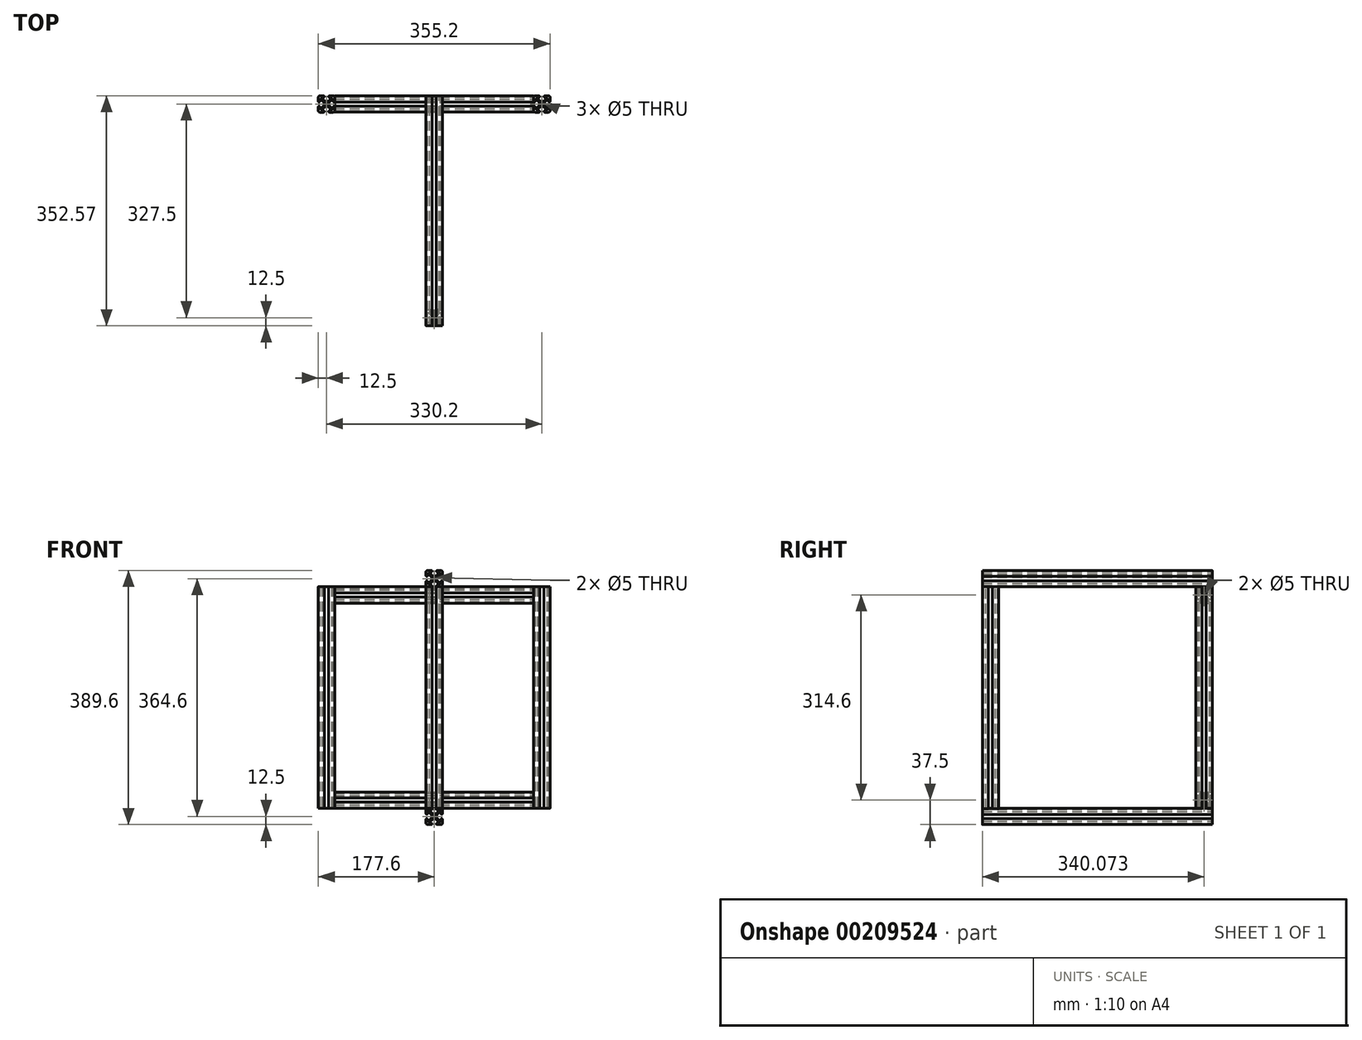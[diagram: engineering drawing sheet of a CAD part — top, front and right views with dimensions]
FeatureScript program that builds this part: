
annotation { "Feature Type Name" : "Feature", "Feature Type Description" : "" }
export const myFeature = defineFeature(function(context is Context, id is Id, definition is map)
    precondition{}
    {
        {
            var Q0;
            Q0=qCreatedBy(makeId("Top.planeOp"),FACE);
            var sketch = newSketch(context, id + "F0", { "sketchPlane" : qUnion([Q0])});
            skCircle(sketch, "E0", {"center": v(0, 0) * mm, "radius": 2.5 * mm});
            skLineSegment(sketch, "E1", {"start": v(0, 0) * mm, "end": v(0, 4.05) * mm, "construction": true});
            skLineSegment(sketch, "E2", {"start": v(0, 0) * mm, "end": v(-4.05, 0) * mm, "construction": true});
            skLineSegment(sketch, "E3", {"start": v(0, 0) * mm, "end": v(-12.5, 12.5) * mm, "construction": true});
            skLineSegment(sketch, "E4", {"start": v(-12.5, 10.36) * mm, "end": v(-12.5, 4.32) * mm});
            skLineSegment(sketch, "E5", {"start": v(-10.36, 12.5) * mm, "end": v(-4.32, 12.5) * mm});
            skLineSegment(sketch, "E6", {"start": v(-4.32, 10.36) * mm, "end": v(-6.26, 10.36) * mm});
            skLineSegment(sketch, "E7", {"start": v(-10.36, 6.26) * mm, "end": v(-10.36, 4.32) * mm});
            skArc(sketch, "E8", {"start": v(-4.32, 12.5) * mm, "mid": v(-3.25, 11.43) * mm, "end": v(-4.32, 10.36) * mm});
            skArc(sketch, "E9", {"start": v(-10.36, 4.32) * mm, "mid": v(-11.43, 3.25) * mm, "end": v(-12.5, 4.32) * mm});
            skLineSegment(sketch, "E10", {"start": v(0, 4.05) * mm, "end": v(-2.1, 4.05) * mm});
            skLineSegment(sketch, "E11", {"start": v(-4.05, 2.1) * mm, "end": v(-4.05, 0) * mm});
            skLineSegment(sketch, "E12", {"start": v(-8.53, 7.02) * mm, "end": v(-4.36, 2.85) * mm});
            skLineSegment(sketch, "E13", {"start": v(-7.02, 8.53) * mm, "end": v(-2.85, 4.36) * mm});
            skLineSegment(sketch, "E14.0.MirrorCS", {"start": v(10.36, 6.26) * mm, "end": v(10.36, 4.32) * mm});
            skLineSegment(sketch, "E14.1.MirrorCS", {"start": v(7.02, 8.53) * mm, "end": v(2.85, 4.36) * mm});
            skArc(sketch, "E14.2.MirrorCS", {"start": v(4.32, 12.5) * mm, "mid": v(3.25, 11.43) * mm, "end": v(4.32, 10.36) * mm});
            skArc(sketch, "E14.3.MirrorCS", {"start": v(10.36, 4.32) * mm, "mid": v(11.43, 3.25) * mm, "end": v(12.5, 4.32) * mm});
            skLineSegment(sketch, "E14.4.MirrorCS", {"start": v(10.36, 12.5) * mm, "end": v(4.32, 12.5) * mm});
            skLineSegment(sketch, "E14.5.MirrorCS", {"start": v(4.32, 10.36) * mm, "end": v(6.26, 10.36) * mm});
            skLineSegment(sketch, "E14.6.MirrorCS", {"start": v(12.5, 10.36) * mm, "end": v(12.5, 4.32) * mm});
            skLineSegment(sketch, "E14.7.MirrorCS", {"start": v(8.53, 7.02) * mm, "end": v(4.36, 2.85) * mm});
            skLineSegment(sketch, "E15.0.MirrorCS", {"start": v(0, 4.05) * mm, "end": v(2.1, 4.05) * mm});
            skLineSegment(sketch, "E16.0.MirrorCS", {"start": v(4.05, 2.1) * mm, "end": v(4.05, 0) * mm});
            skLineSegment(sketch, "E17.0.MirrorCS", {"start": v(10.36, -12.5) * mm, "end": v(4.32, -12.5) * mm});
            skLineSegment(sketch, "E17.1.MirrorCS", {"start": v(12.5, -10.36) * mm, "end": v(12.5, -4.32) * mm});
            skArc(sketch, "E17.2.MirrorCS", {"start": v(4.32, -12.5) * mm, "mid": v(3.25, -11.43) * mm, "end": v(4.32, -10.36) * mm});
            skLineSegment(sketch, "E17.3.MirrorCS", {"start": v(-7.02, -8.53) * mm, "end": v(-2.85, -4.36) * mm});
            skLineSegment(sketch, "E17.4.MirrorCS", {"start": v(7.02, -8.53) * mm, "end": v(2.85, -4.36) * mm});
            skLineSegment(sketch, "E17.5.MirrorCS", {"start": v(10.36, -6.26) * mm, "end": v(10.36, -4.32) * mm});
            skLineSegment(sketch, "E17.6.MirrorCS", {"start": v(8.53, -7.02) * mm, "end": v(4.36, -2.85) * mm});
            skLineSegment(sketch, "E17.7.MirrorCS", {"start": v(-10.36, -12.5) * mm, "end": v(-4.32, -12.5) * mm});
            skLineSegment(sketch, "E17.8.MirrorCS", {"start": v(-4.32, -10.36) * mm, "end": v(-6.26, -10.36) * mm});
            skLineSegment(sketch, "E17.9.MirrorCS", {"start": v(4.32, -10.36) * mm, "end": v(6.26, -10.36) * mm});
            skArc(sketch, "E17.10.MirrorCS", {"start": v(10.36, -4.32) * mm, "mid": v(11.43, -3.25) * mm, "end": v(12.5, -4.32) * mm});
            skLineSegment(sketch, "E17.11.MirrorCS", {"start": v(-12.5, -10.36) * mm, "end": v(-12.5, -4.32) * mm});
            skLineSegment(sketch, "E17.12.MirrorCS", {"start": v(0, -4.05) * mm, "end": v(2.1, -4.05) * mm});
            skArc(sketch, "E17.13.MirrorCS", {"start": v(-4.32, -12.5) * mm, "mid": v(-3.25, -11.43) * mm, "end": v(-4.32, -10.36) * mm});
            skLineSegment(sketch, "E17.14.MirrorCS", {"start": v(-8.53, -7.02) * mm, "end": v(-4.36, -2.85) * mm});
            skArc(sketch, "E17.15.MirrorCS", {"start": v(-10.36, -4.32) * mm, "mid": v(-11.43, -3.25) * mm, "end": v(-12.5, -4.32) * mm});
            skLineSegment(sketch, "E17.16.MirrorCS", {"start": v(-10.36, -6.26) * mm, "end": v(-10.36, -4.32) * mm});
            skLineSegment(sketch, "E17.17.MirrorCS", {"start": v(0, -4.05) * mm, "end": v(-2.1, -4.05) * mm});
            skLineSegment(sketch, "E18.0.MirrorCS", {"start": v(4.05, -2.1) * mm, "end": v(4.05, 0) * mm});
            skLineSegment(sketch, "E19.0.MirrorCS", {"start": v(-4.05, -2.1) * mm, "end": v(-4.05, 0) * mm});
            skPoint(sketch, "E20.visualSharp", {"position": v(-12.5, 12.5) * mm});
            skArc(sketch, "E20.filletArc", {"start": v(-10.36, 12.5) * mm, "mid": v(-11.87, 11.87) * mm, "end": v(-12.5, 10.36) * mm});
            skPoint(sketch, "E21.visualSharp", {"position": v(12.5, 12.5) * mm});
            skArc(sketch, "E21.filletArc", {"start": v(12.5, 10.36) * mm, "mid": v(11.87, 11.87) * mm, "end": v(10.36, 12.5) * mm});
            skPoint(sketch, "E22.visualSharp", {"position": v(12.5, -12.5) * mm});
            skArc(sketch, "E22.filletArc", {"start": v(10.36, -12.5) * mm, "mid": v(11.87, -11.87) * mm, "end": v(12.5, -10.36) * mm});
            skPoint(sketch, "E23.visualSharp", {"position": v(-12.5, -12.5) * mm});
            skArc(sketch, "E23.filletArc", {"start": v(-12.5, -10.36) * mm, "mid": v(-11.87, -11.87) * mm, "end": v(-10.36, -12.5) * mm});
            skPoint(sketch, "E24.visualSharp", {"position": v(4.05, 4.05) * mm});
            skPoint(sketch, "E25.visualSharp", {"position": v(-10.36, 8.85) * mm});
            skArc(sketch, "E25.filletArc", {"start": v(-8.53, 7.02) * mm, "mid": v(-9.7, 7.25) * mm, "end": v(-10.36, 6.26) * mm});
            skPoint(sketch, "E26.visualSharp", {"position": v(-8.85, 10.36) * mm});
            skArc(sketch, "E26.filletArc", {"start": v(-6.26, 10.36) * mm, "mid": v(-7.25, 9.7) * mm, "end": v(-7.02, 8.53) * mm});
            skPoint(sketch, "E27.visualSharp", {"position": v(8.85, 10.36) * mm});
            skArc(sketch, "E27.filletArc", {"start": v(7.02, 8.53) * mm, "mid": v(7.25, 9.7) * mm, "end": v(6.26, 10.36) * mm});
            skPoint(sketch, "E28.visualSharp", {"position": v(10.36, 8.85) * mm});
            skArc(sketch, "E28.filletArc", {"start": v(10.36, 6.26) * mm, "mid": v(9.7, 7.25) * mm, "end": v(8.53, 7.02) * mm});
            skPoint(sketch, "E29.visualSharp", {"position": v(10.36, -8.85) * mm});
            skArc(sketch, "E29.filletArc", {"start": v(8.53, -7.02) * mm, "mid": v(9.7, -7.25) * mm, "end": v(10.36, -6.26) * mm});
            skPoint(sketch, "E30.visualSharp", {"position": v(8.85, -10.36) * mm});
            skArc(sketch, "E30.filletArc", {"start": v(6.26, -10.36) * mm, "mid": v(7.25, -9.7) * mm, "end": v(7.02, -8.53) * mm});
            skPoint(sketch, "E31.visualSharp", {"position": v(-8.85, -10.36) * mm});
            skArc(sketch, "E31.filletArc", {"start": v(-7.02, -8.53) * mm, "mid": v(-7.25, -9.7) * mm, "end": v(-6.26, -10.36) * mm});
            skPoint(sketch, "E32.visualSharp", {"position": v(-10.36, -8.85) * mm});
            skArc(sketch, "E32.filletArc", {"start": v(-10.36, -6.26) * mm, "mid": v(-9.7, -7.25) * mm, "end": v(-8.53, -7.02) * mm});
            skPoint(sketch, "E33.orphan", {"position": v(-4.05, 4.05) * mm});
            skPoint(sketch, "E34.orphan", {"position": v(4.05, -4.05) * mm});
            skPoint(sketch, "E35.orphan", {"position": v(-4.05, -4.05) * mm});
            skPoint(sketch, "E36.visualSharp", {"position": v(-2.54, 4.05) * mm});
            skArc(sketch, "E36.filletArc", {"start": v(-2.85, 4.36) * mm, "mid": v(-2.5, 4.13) * mm, "end": v(-2.1, 4.05) * mm});
            skPoint(sketch, "E37.visualSharp", {"position": v(2.54, 4.05) * mm});
            skArc(sketch, "E37.filletArc", {"start": v(2.1, 4.05) * mm, "mid": v(2.5, 4.13) * mm, "end": v(2.85, 4.36) * mm});
            skPoint(sketch, "E38.visualSharp", {"position": v(-4.05, 2.54) * mm});
            skArc(sketch, "E38.filletArc", {"start": v(-4.05, 2.1) * mm, "mid": v(-4.13, 2.5) * mm, "end": v(-4.36, 2.85) * mm});
            skPoint(sketch, "E39.visualSharp", {"position": v(-4.05, -2.54) * mm});
            skArc(sketch, "E39.filletArc", {"start": v(-4.36, -2.85) * mm, "mid": v(-4.13, -2.5) * mm, "end": v(-4.05, -2.1) * mm});
            skPoint(sketch, "E40.visualSharp", {"position": v(-2.54, -4.05) * mm});
            skArc(sketch, "E40.filletArc", {"start": v(-2.1, -4.05) * mm, "mid": v(-2.5, -4.13) * mm, "end": v(-2.85, -4.36) * mm});
            skPoint(sketch, "E41.visualSharp", {"position": v(2.54, -4.05) * mm});
            skArc(sketch, "E41.filletArc", {"start": v(2.85, -4.36) * mm, "mid": v(2.5, -4.13) * mm, "end": v(2.1, -4.05) * mm});
            skPoint(sketch, "E42.visualSharp", {"position": v(4.05, -2.54) * mm});
            skArc(sketch, "E42.filletArc", {"start": v(4.05, -2.1) * mm, "mid": v(4.13, -2.5) * mm, "end": v(4.36, -2.85) * mm});
            skPoint(sketch, "E43.visualSharp", {"position": v(4.05, 2.54) * mm});
            skArc(sketch, "E43.filletArc", {"start": v(4.36, 2.85) * mm, "mid": v(4.13, 2.5) * mm, "end": v(4.05, 2.1) * mm});
            skSolve(sketch);
        }
        {
            var Q0;
            Q0=qSketchRegion(id+"F0",true);
            extrude(context, id + "F1", {"entities" : qUnion([Q0]), "endBound" : BoundingType.SYMMETRIC, "depth" : 340 * mm});
        }
        {
            var Q0;
            Q0=qCreatedBy(makeId("Top.planeOp"),FACE);
            var sketch = newSketch(context, id + "F2", { "sketchPlane" : qUnion([Q0])});
            skCircle(sketch, "E44", {"center": v(330.2, 0) * mm, "radius": 2.5 * mm});
            skLineSegment(sketch, "E45", {"start": v(330.2, 0) * mm, "end": v(330.2, 4.05) * mm, "construction": true});
            skLineSegment(sketch, "E46", {"start": v(330.2, 0) * mm, "end": v(326.15, 0) * mm, "construction": true});
            skLineSegment(sketch, "E47", {"start": v(330.2, 0) * mm, "end": v(317.7, 12.5) * mm, "construction": true});
            skLineSegment(sketch, "E48", {"start": v(317.7, 10.36) * mm, "end": v(317.7, 4.32) * mm});
            skLineSegment(sketch, "E49", {"start": v(319.84, 12.5) * mm, "end": v(325.88, 12.5) * mm});
            skLineSegment(sketch, "E50", {"start": v(325.88, 10.36) * mm, "end": v(323.94, 10.36) * mm});
            skLineSegment(sketch, "E51", {"start": v(319.84, 6.26) * mm, "end": v(319.84, 4.32) * mm});
            skArc(sketch, "E52", {"start": v(325.88, 12.5) * mm, "mid": v(326.95, 11.43) * mm, "end": v(325.88, 10.36) * mm});
            skArc(sketch, "E53", {"start": v(319.84, 4.32) * mm, "mid": v(318.77, 3.25) * mm, "end": v(317.7, 4.32) * mm});
            skLineSegment(sketch, "E54", {"start": v(330.2, 4.05) * mm, "end": v(328.1, 4.05) * mm});
            skLineSegment(sketch, "E55", {"start": v(326.15, 2.1) * mm, "end": v(326.15, 0) * mm});
            skLineSegment(sketch, "E56", {"start": v(321.67, 7.02) * mm, "end": v(325.84, 2.85) * mm});
            skLineSegment(sketch, "E57", {"start": v(323.18, 8.53) * mm, "end": v(327.35, 4.36) * mm});
            skLineSegment(sketch, "E58.0.MirrorCS", {"start": v(340.56, 6.26) * mm, "end": v(340.56, 4.32) * mm});
            skLineSegment(sketch, "E58.1.MirrorCS", {"start": v(337.22, 8.53) * mm, "end": v(333.05, 4.36) * mm});
            skArc(sketch, "E58.2.MirrorCS", {"start": v(334.52, 12.5) * mm, "mid": v(333.45, 11.43) * mm, "end": v(334.52, 10.36) * mm});
            skArc(sketch, "E58.3.MirrorCS", {"start": v(340.56, 4.32) * mm, "mid": v(341.63, 3.25) * mm, "end": v(342.7, 4.32) * mm});
            skLineSegment(sketch, "E58.4.MirrorCS", {"start": v(340.56, 12.5) * mm, "end": v(334.52, 12.5) * mm});
            skLineSegment(sketch, "E58.5.MirrorCS", {"start": v(334.52, 10.36) * mm, "end": v(336.46, 10.36) * mm});
            skLineSegment(sketch, "E58.6.MirrorCS", {"start": v(342.7, 10.36) * mm, "end": v(342.7, 4.32) * mm});
            skLineSegment(sketch, "E58.7.MirrorCS", {"start": v(338.73, 7.02) * mm, "end": v(334.56, 2.85) * mm});
            skLineSegment(sketch, "E59.0.MirrorCS", {"start": v(330.2, 4.05) * mm, "end": v(332.3, 4.05) * mm});
            skLineSegment(sketch, "E60.0.MirrorCS", {"start": v(334.25, 2.1) * mm, "end": v(334.25, 0) * mm});
            skLineSegment(sketch, "E61.0.MirrorCS", {"start": v(340.56, -12.5) * mm, "end": v(334.52, -12.5) * mm});
            skLineSegment(sketch, "E61.1.MirrorCS", {"start": v(342.7, -10.36) * mm, "end": v(342.7, -4.32) * mm});
            skArc(sketch, "E61.2.MirrorCS", {"start": v(334.52, -12.5) * mm, "mid": v(333.45, -11.43) * mm, "end": v(334.52, -10.36) * mm});
            skLineSegment(sketch, "E61.3.MirrorCS", {"start": v(323.18, -8.53) * mm, "end": v(327.35, -4.36) * mm});
            skLineSegment(sketch, "E61.4.MirrorCS", {"start": v(337.22, -8.53) * mm, "end": v(333.05, -4.36) * mm});
            skLineSegment(sketch, "E61.5.MirrorCS", {"start": v(340.56, -6.26) * mm, "end": v(340.56, -4.32) * mm});
            skLineSegment(sketch, "E61.6.MirrorCS", {"start": v(338.73, -7.02) * mm, "end": v(334.56, -2.85) * mm});
            skLineSegment(sketch, "E61.7.MirrorCS", {"start": v(319.84, -12.5) * mm, "end": v(325.88, -12.5) * mm});
            skLineSegment(sketch, "E61.8.MirrorCS", {"start": v(325.88, -10.36) * mm, "end": v(323.94, -10.36) * mm});
            skLineSegment(sketch, "E61.9.MirrorCS", {"start": v(334.52, -10.36) * mm, "end": v(336.46, -10.36) * mm});
            skArc(sketch, "E61.10.MirrorCS", {"start": v(340.56, -4.32) * mm, "mid": v(341.63, -3.25) * mm, "end": v(342.7, -4.32) * mm});
            skLineSegment(sketch, "E61.11.MirrorCS", {"start": v(317.7, -10.36) * mm, "end": v(317.7, -4.32) * mm});
            skLineSegment(sketch, "E61.12.MirrorCS", {"start": v(330.2, -4.05) * mm, "end": v(332.3, -4.05) * mm});
            skArc(sketch, "E61.13.MirrorCS", {"start": v(325.88, -12.5) * mm, "mid": v(326.95, -11.43) * mm, "end": v(325.88, -10.36) * mm});
            skLineSegment(sketch, "E61.14.MirrorCS", {"start": v(321.67, -7.02) * mm, "end": v(325.84, -2.85) * mm});
            skArc(sketch, "E61.15.MirrorCS", {"start": v(319.84, -4.32) * mm, "mid": v(318.77, -3.25) * mm, "end": v(317.7, -4.32) * mm});
            skLineSegment(sketch, "E61.16.MirrorCS", {"start": v(319.84, -6.26) * mm, "end": v(319.84, -4.32) * mm});
            skLineSegment(sketch, "E61.17.MirrorCS", {"start": v(330.2, -4.05) * mm, "end": v(328.1, -4.05) * mm});
            skLineSegment(sketch, "E62.0.MirrorCS", {"start": v(334.25, -2.1) * mm, "end": v(334.25, 0) * mm});
            skLineSegment(sketch, "E63.0.MirrorCS", {"start": v(326.15, -2.1) * mm, "end": v(326.15, 0) * mm});
            skPoint(sketch, "E64.visualSharp", {"position": v(317.7, 12.5) * mm});
            skArc(sketch, "E64.filletArc", {"start": v(319.84, 12.5) * mm, "mid": v(318.33, 11.87) * mm, "end": v(317.7, 10.36) * mm});
            skPoint(sketch, "E65.visualSharp", {"position": v(342.7, 12.5) * mm});
            skArc(sketch, "E65.filletArc", {"start": v(342.7, 10.36) * mm, "mid": v(342.07, 11.87) * mm, "end": v(340.56, 12.5) * mm});
            skPoint(sketch, "E66.visualSharp", {"position": v(342.7, -12.5) * mm});
            skArc(sketch, "E66.filletArc", {"start": v(340.56, -12.5) * mm, "mid": v(342.07, -11.87) * mm, "end": v(342.7, -10.36) * mm});
            skPoint(sketch, "E67.visualSharp", {"position": v(317.7, -12.5) * mm});
            skArc(sketch, "E67.filletArc", {"start": v(317.7, -10.36) * mm, "mid": v(318.33, -11.87) * mm, "end": v(319.84, -12.5) * mm});
            skPoint(sketch, "E68.visualSharp", {"position": v(334.25, 4.05) * mm});
            skPoint(sketch, "E69.visualSharp", {"position": v(319.84, 8.85) * mm});
            skArc(sketch, "E69.filletArc", {"start": v(321.67, 7.02) * mm, "mid": v(320.5, 7.25) * mm, "end": v(319.84, 6.26) * mm});
            skPoint(sketch, "E70.visualSharp", {"position": v(321.35, 10.36) * mm});
            skArc(sketch, "E70.filletArc", {"start": v(323.94, 10.36) * mm, "mid": v(322.95, 9.7) * mm, "end": v(323.18, 8.53) * mm});
            skPoint(sketch, "E71.visualSharp", {"position": v(339.05, 10.36) * mm});
            skArc(sketch, "E71.filletArc", {"start": v(337.22, 8.53) * mm, "mid": v(337.45, 9.7) * mm, "end": v(336.46, 10.36) * mm});
            skPoint(sketch, "E72.visualSharp", {"position": v(340.56, 8.85) * mm});
            skArc(sketch, "E72.filletArc", {"start": v(340.56, 6.26) * mm, "mid": v(339.9, 7.25) * mm, "end": v(338.73, 7.02) * mm});
            skPoint(sketch, "E73.visualSharp", {"position": v(340.56, -8.85) * mm});
            skArc(sketch, "E73.filletArc", {"start": v(338.73, -7.02) * mm, "mid": v(339.9, -7.25) * mm, "end": v(340.56, -6.26) * mm});
            skPoint(sketch, "E74.visualSharp", {"position": v(339.05, -10.36) * mm});
            skArc(sketch, "E74.filletArc", {"start": v(336.46, -10.36) * mm, "mid": v(337.45, -9.7) * mm, "end": v(337.22, -8.53) * mm});
            skPoint(sketch, "E75.visualSharp", {"position": v(321.35, -10.36) * mm});
            skArc(sketch, "E75.filletArc", {"start": v(323.18, -8.53) * mm, "mid": v(322.95, -9.7) * mm, "end": v(323.94, -10.36) * mm});
            skPoint(sketch, "E76.visualSharp", {"position": v(319.84, -8.85) * mm});
            skArc(sketch, "E76.filletArc", {"start": v(319.84, -6.26) * mm, "mid": v(320.5, -7.25) * mm, "end": v(321.67, -7.02) * mm});
            skPoint(sketch, "E77.orphan", {"position": v(326.15, 4.05) * mm});
            skPoint(sketch, "E78.orphan", {"position": v(334.25, -4.05) * mm});
            skPoint(sketch, "E79.orphan", {"position": v(326.15, -4.05) * mm});
            skPoint(sketch, "E80.visualSharp", {"position": v(327.66, 4.05) * mm});
            skArc(sketch, "E80.filletArc", {"start": v(327.35, 4.36) * mm, "mid": v(327.7, 4.13) * mm, "end": v(328.1, 4.05) * mm});
            skPoint(sketch, "E81.visualSharp", {"position": v(332.74, 4.05) * mm});
            skArc(sketch, "E81.filletArc", {"start": v(332.3, 4.05) * mm, "mid": v(332.7, 4.13) * mm, "end": v(333.05, 4.36) * mm});
            skPoint(sketch, "E82.visualSharp", {"position": v(326.15, 2.54) * mm});
            skArc(sketch, "E82.filletArc", {"start": v(326.15, 2.1) * mm, "mid": v(326.07, 2.5) * mm, "end": v(325.84, 2.85) * mm});
            skPoint(sketch, "E83.visualSharp", {"position": v(326.15, -2.54) * mm});
            skArc(sketch, "E83.filletArc", {"start": v(325.84, -2.85) * mm, "mid": v(326.07, -2.5) * mm, "end": v(326.15, -2.1) * mm});
            skPoint(sketch, "E84.visualSharp", {"position": v(327.66, -4.05) * mm});
            skArc(sketch, "E84.filletArc", {"start": v(328.1, -4.05) * mm, "mid": v(327.7, -4.13) * mm, "end": v(327.35, -4.36) * mm});
            skPoint(sketch, "E85.visualSharp", {"position": v(332.74, -4.05) * mm});
            skArc(sketch, "E85.filletArc", {"start": v(333.05, -4.36) * mm, "mid": v(332.7, -4.13) * mm, "end": v(332.3, -4.05) * mm});
            skPoint(sketch, "E86.visualSharp", {"position": v(334.25, -2.54) * mm});
            skArc(sketch, "E86.filletArc", {"start": v(334.25, -2.1) * mm, "mid": v(334.33, -2.5) * mm, "end": v(334.56, -2.85) * mm});
            skPoint(sketch, "E87.visualSharp", {"position": v(334.25, 2.54) * mm});
            skArc(sketch, "E87.filletArc", {"start": v(334.56, 2.85) * mm, "mid": v(334.33, 2.5) * mm, "end": v(334.25, 2.1) * mm});
            skSolve(sketch);
        }
        {
            var Q0;
            Q0=makeQuery(id+"F2.imprint","IMPRINT",FACE,{"disambiguationData":[TD([[makeQuery(id+"F2.imprint","IMPRINT",EDGE,{"derivedFrom":sQuery(id+"F2.wireOp",EDGE,"E44")}),-1.0]])]});
            extrude(context, id + "F3", {"entities" : qUnion([Q0]), "endBound" : BoundingType.SYMMETRIC, "depth" : 340 * mm});
        }
        {
            var Q0;
            Q0=makeQuery(id+"F3.opExtrude","SWEPT_FACE",FACE,{"disambiguationData":[OSD([sQuery(id+"F2.wireOp",EDGE,"E48")])]});
            var sketch = newSketch(context, id + "F4", { "sketchPlane" : qUnion([Q0])});
            skCircle(sketch, "E88", {"center": v(-0.07, -157.3) * mm, "radius": 2.5 * mm});
            skLineSegment(sketch, "E89", {"start": v(-0.07, -157.3) * mm, "end": v(-0.07, -153.25) * mm, "construction": true});
            skLineSegment(sketch, "E90", {"start": v(-0.07, -157.3) * mm, "end": v(-4.12, -157.3) * mm, "construction": true});
            skLineSegment(sketch, "E91", {"start": v(-0.07, -157.3) * mm, "end": v(-12.57, -144.8) * mm, "construction": true});
            skLineSegment(sketch, "E92", {"start": v(-12.57, -146.94) * mm, "end": v(-12.57, -152.98) * mm});
            skLineSegment(sketch, "E93", {"start": v(-10.43, -144.8) * mm, "end": v(-4.4, -144.8) * mm});
            skLineSegment(sketch, "E94", {"start": v(-4.4, -146.94) * mm, "end": v(-6.34, -146.94) * mm});
            skLineSegment(sketch, "E95", {"start": v(-10.43, -151.04) * mm, "end": v(-10.43, -152.98) * mm});
            skArc(sketch, "E96", {"start": v(-4.4, -144.8) * mm, "mid": v(-3.32, -145.87) * mm, "end": v(-4.4, -146.94) * mm});
            skArc(sketch, "E97", {"start": v(-10.43, -152.98) * mm, "mid": v(-11.5, -154.05) * mm, "end": v(-12.57, -152.98) * mm});
            skLineSegment(sketch, "E98", {"start": v(-0.07, -153.25) * mm, "end": v(-2.17, -153.25) * mm});
            skLineSegment(sketch, "E99", {"start": v(-4.12, -155.2) * mm, "end": v(-4.12, -157.3) * mm});
            skLineSegment(sketch, "E100", {"start": v(-8.6, -150.28) * mm, "end": v(-4.44, -154.45) * mm});
            skLineSegment(sketch, "E101", {"start": v(-7.1, -148.77) * mm, "end": v(-2.92, -152.94) * mm});
            skLineSegment(sketch, "E102.0.MirrorCS", {"start": v(10.29, -151.04) * mm, "end": v(10.29, -152.98) * mm});
            skLineSegment(sketch, "E102.1.MirrorCS", {"start": v(6.95, -148.77) * mm, "end": v(2.78, -152.94) * mm});
            skArc(sketch, "E102.2.MirrorCS", {"start": v(4.25, -144.8) * mm, "mid": v(3.18, -145.87) * mm, "end": v(4.25, -146.94) * mm});
            skArc(sketch, "E102.3.MirrorCS", {"start": v(10.29, -152.98) * mm, "mid": v(11.36, -154.05) * mm, "end": v(12.43, -152.98) * mm});
            skLineSegment(sketch, "E102.4.MirrorCS", {"start": v(10.29, -144.8) * mm, "end": v(4.25, -144.8) * mm});
            skLineSegment(sketch, "E102.5.MirrorCS", {"start": v(4.25, -146.94) * mm, "end": v(6.2, -146.94) * mm});
            skLineSegment(sketch, "E102.6.MirrorCS", {"start": v(12.43, -146.94) * mm, "end": v(12.43, -152.98) * mm});
            skLineSegment(sketch, "E102.7.MirrorCS", {"start": v(8.46, -150.28) * mm, "end": v(4.3, -154.45) * mm});
            skLineSegment(sketch, "E103.0.MirrorCS", {"start": v(-0.07, -153.25) * mm, "end": v(2.02, -153.25) * mm});
            skLineSegment(sketch, "E104.0.MirrorCS", {"start": v(3.98, -155.2) * mm, "end": v(3.98, -157.3) * mm});
            skLineSegment(sketch, "E105.0.MirrorCS", {"start": v(10.29, -169.8) * mm, "end": v(4.25, -169.8) * mm});
            skLineSegment(sketch, "E105.1.MirrorCS", {"start": v(12.43, -167.66) * mm, "end": v(12.43, -161.62) * mm});
            skArc(sketch, "E105.2.MirrorCS", {"start": v(4.25, -169.8) * mm, "mid": v(3.18, -168.73) * mm, "end": v(4.25, -167.66) * mm});
            skLineSegment(sketch, "E105.3.MirrorCS", {"start": v(-7.1, -165.83) * mm, "end": v(-2.92, -161.66) * mm});
            skLineSegment(sketch, "E105.4.MirrorCS", {"start": v(6.95, -165.83) * mm, "end": v(2.78, -161.66) * mm});
            skLineSegment(sketch, "E105.5.MirrorCS", {"start": v(10.29, -163.56) * mm, "end": v(10.29, -161.62) * mm});
            skLineSegment(sketch, "E105.6.MirrorCS", {"start": v(8.46, -164.32) * mm, "end": v(4.3, -160.15) * mm});
            skLineSegment(sketch, "E105.7.MirrorCS", {"start": v(-10.43, -169.8) * mm, "end": v(-4.4, -169.8) * mm});
            skLineSegment(sketch, "E105.8.MirrorCS", {"start": v(-4.4, -167.66) * mm, "end": v(-6.34, -167.66) * mm});
            skLineSegment(sketch, "E105.9.MirrorCS", {"start": v(4.25, -167.66) * mm, "end": v(6.2, -167.66) * mm});
            skArc(sketch, "E105.10.MirrorCS", {"start": v(10.29, -161.62) * mm, "mid": v(11.36, -160.55) * mm, "end": v(12.43, -161.62) * mm});
            skLineSegment(sketch, "E105.11.MirrorCS", {"start": v(-12.57, -167.66) * mm, "end": v(-12.57, -161.62) * mm});
            skLineSegment(sketch, "E105.12.MirrorCS", {"start": v(-0.07, -161.35) * mm, "end": v(2.02, -161.35) * mm});
            skArc(sketch, "E105.13.MirrorCS", {"start": v(-4.4, -169.8) * mm, "mid": v(-3.32, -168.73) * mm, "end": v(-4.4, -167.66) * mm});
            skLineSegment(sketch, "E105.14.MirrorCS", {"start": v(-8.6, -164.32) * mm, "end": v(-4.44, -160.15) * mm});
            skArc(sketch, "E105.15.MirrorCS", {"start": v(-10.43, -161.62) * mm, "mid": v(-11.5, -160.55) * mm, "end": v(-12.57, -161.62) * mm});
            skLineSegment(sketch, "E105.16.MirrorCS", {"start": v(-10.43, -163.56) * mm, "end": v(-10.43, -161.62) * mm});
            skLineSegment(sketch, "E105.17.MirrorCS", {"start": v(-0.07, -161.35) * mm, "end": v(-2.17, -161.35) * mm});
            skLineSegment(sketch, "E106.0.MirrorCS", {"start": v(3.98, -159.4) * mm, "end": v(3.98, -157.3) * mm});
            skLineSegment(sketch, "E107.0.MirrorCS", {"start": v(-4.12, -159.4) * mm, "end": v(-4.12, -157.3) * mm});
            skPoint(sketch, "E108.visualSharp", {"position": v(-12.57, -144.8) * mm});
            skArc(sketch, "E108.filletArc", {"start": v(-10.43, -144.8) * mm, "mid": v(-11.95, -145.43) * mm, "end": v(-12.57, -146.94) * mm});
            skPoint(sketch, "E109.visualSharp", {"position": v(12.43, -144.8) * mm});
            skArc(sketch, "E109.filletArc", {"start": v(12.43, -146.94) * mm, "mid": v(11.8, -145.43) * mm, "end": v(10.29, -144.8) * mm});
            skPoint(sketch, "E110.visualSharp", {"position": v(12.43, -169.8) * mm});
            skArc(sketch, "E110.filletArc", {"start": v(10.29, -169.8) * mm, "mid": v(11.8, -169.17) * mm, "end": v(12.43, -167.66) * mm});
            skPoint(sketch, "E111.visualSharp", {"position": v(-12.57, -169.8) * mm});
            skArc(sketch, "E111.filletArc", {"start": v(-12.57, -167.66) * mm, "mid": v(-11.95, -169.17) * mm, "end": v(-10.43, -169.8) * mm});
            skPoint(sketch, "E112.visualSharp", {"position": v(3.98, -153.25) * mm});
            skPoint(sketch, "E113.visualSharp", {"position": v(-10.43, -148.45) * mm});
            skArc(sketch, "E113.filletArc", {"start": v(-8.6, -150.28) * mm, "mid": v(-9.77, -150.05) * mm, "end": v(-10.43, -151.04) * mm});
            skPoint(sketch, "E114.visualSharp", {"position": v(-8.92, -146.94) * mm});
            skArc(sketch, "E114.filletArc", {"start": v(-6.34, -146.94) * mm, "mid": v(-7.33, -147.6) * mm, "end": v(-7.1, -148.77) * mm});
            skPoint(sketch, "E115.visualSharp", {"position": v(8.77, -146.94) * mm});
            skArc(sketch, "E115.filletArc", {"start": v(6.95, -148.77) * mm, "mid": v(7.18, -147.6) * mm, "end": v(6.2, -146.94) * mm});
            skPoint(sketch, "E116.visualSharp", {"position": v(10.29, -148.45) * mm});
            skArc(sketch, "E116.filletArc", {"start": v(10.29, -151.04) * mm, "mid": v(9.63, -150.05) * mm, "end": v(8.46, -150.28) * mm});
            skPoint(sketch, "E117.visualSharp", {"position": v(10.29, -166.15) * mm});
            skArc(sketch, "E117.filletArc", {"start": v(8.46, -164.32) * mm, "mid": v(9.63, -164.55) * mm, "end": v(10.29, -163.56) * mm});
            skPoint(sketch, "E118.visualSharp", {"position": v(8.77, -167.66) * mm});
            skArc(sketch, "E118.filletArc", {"start": v(6.2, -167.66) * mm, "mid": v(7.18, -167) * mm, "end": v(6.95, -165.83) * mm});
            skPoint(sketch, "E119.visualSharp", {"position": v(-8.92, -167.66) * mm});
            skArc(sketch, "E119.filletArc", {"start": v(-7.1, -165.83) * mm, "mid": v(-7.33, -167) * mm, "end": v(-6.34, -167.66) * mm});
            skPoint(sketch, "E120.visualSharp", {"position": v(-10.43, -166.15) * mm});
            skArc(sketch, "E120.filletArc", {"start": v(-10.43, -163.56) * mm, "mid": v(-9.77, -164.55) * mm, "end": v(-8.6, -164.32) * mm});
            skPoint(sketch, "E121.orphan", {"position": v(-4.12, -153.25) * mm});
            skPoint(sketch, "E122.orphan", {"position": v(3.98, -161.35) * mm});
            skPoint(sketch, "E123.orphan", {"position": v(-4.12, -161.35) * mm});
            skPoint(sketch, "E124.visualSharp", {"position": v(-2.6, -153.25) * mm});
            skArc(sketch, "E124.filletArc", {"start": v(-2.92, -152.94) * mm, "mid": v(-2.58, -153.17) * mm, "end": v(-2.17, -153.25) * mm});
            skPoint(sketch, "E125.visualSharp", {"position": v(2.46, -153.25) * mm});
            skArc(sketch, "E125.filletArc", {"start": v(2.02, -153.25) * mm, "mid": v(2.43, -153.17) * mm, "end": v(2.78, -152.94) * mm});
            skPoint(sketch, "E126.visualSharp", {"position": v(-4.12, -154.76) * mm});
            skArc(sketch, "E126.filletArc", {"start": v(-4.12, -155.2) * mm, "mid": v(-4.2, -154.8) * mm, "end": v(-4.44, -154.45) * mm});
            skPoint(sketch, "E127.visualSharp", {"position": v(-4.12, -159.84) * mm});
            skArc(sketch, "E127.filletArc", {"start": v(-4.44, -160.15) * mm, "mid": v(-4.2, -159.8) * mm, "end": v(-4.12, -159.4) * mm});
            skPoint(sketch, "E128.visualSharp", {"position": v(-2.6, -161.35) * mm});
            skArc(sketch, "E128.filletArc", {"start": v(-2.17, -161.35) * mm, "mid": v(-2.58, -161.43) * mm, "end": v(-2.92, -161.66) * mm});
            skPoint(sketch, "E129.visualSharp", {"position": v(2.46, -161.35) * mm});
            skArc(sketch, "E129.filletArc", {"start": v(2.78, -161.66) * mm, "mid": v(2.43, -161.43) * mm, "end": v(2.02, -161.35) * mm});
            skPoint(sketch, "E130.visualSharp", {"position": v(3.98, -159.84) * mm});
            skArc(sketch, "E130.filletArc", {"start": v(3.98, -159.4) * mm, "mid": v(4.06, -159.8) * mm, "end": v(4.3, -160.15) * mm});
            skPoint(sketch, "E131.visualSharp", {"position": v(3.98, -154.76) * mm});
            skArc(sketch, "E131.filletArc", {"start": v(4.3, -154.45) * mm, "mid": v(4.06, -154.8) * mm, "end": v(3.98, -155.2) * mm});
            skSolve(sketch);
        }
        {
            var Q0;
            Q0=qSketchRegion(id+"F4",true);
            var Q1;
            Q1=makeQuery(id+"F1.opExtrude","SWEPT_FACE",FACE,{"disambiguationData":[OSD([sQuery(id+"F0.wireOp",EDGE,"E14.6.MirrorCS")])]});
            extrude(context, id + "F5", {"entities" : qUnion([Q0]), "endBound" : BoundingType.UP_TO_SURFACE, "endBoundEntityFace" : qUnion([Q1]), "depth" : 25.4 * mm});
        }
        {
            var Q0;
            Q0=makeQuery(id+"F5.opExtrude","SWEPT_BODY",BODY,{"disambiguationData":[OSD([sQuery(id+"F4.wireOp",EDGE,"E88"),sQuery(id+"F4.wireOp",EDGE,"E92"),sQuery(id+"F4.wireOp",EDGE,"E93"),sQuery(id+"F4.wireOp",EDGE,"E94"),sQuery(id+"F4.wireOp",EDGE,"E95"),sQuery(id+"F4.wireOp",EDGE,"E96"),sQuery(id+"F4.wireOp",EDGE,"E97"),sQuery(id+"F4.wireOp",EDGE,"E99"),sQuery(id+"F4.wireOp",EDGE,"E100"),sQuery(id+"F4.wireOp",EDGE,"E101"),sQuery(id+"F4.wireOp",EDGE,"E102.0.MirrorCS"),sQuery(id+"F4.wireOp",EDGE,"E102.1.MirrorCS"),sQuery(id+"F4.wireOp",EDGE,"E102.2.MirrorCS"),sQuery(id+"F4.wireOp",EDGE,"E102.3.MirrorCS"),sQuery(id+"F4.wireOp",EDGE,"E102.4.MirrorCS"),sQuery(id+"F4.wireOp",EDGE,"E102.5.MirrorCS"),sQuery(id+"F4.wireOp",EDGE,"E102.6.MirrorCS"),sQuery(id+"F4.wireOp",EDGE,"E102.7.MirrorCS"),sQuery(id+"F4.wireOp",EDGE,"E103.0.MirrorCS"),sQuery(id+"F4.wireOp",EDGE,"E105.0.MirrorCS"),sQuery(id+"F4.wireOp",EDGE,"E105.1.MirrorCS"),sQuery(id+"F4.wireOp",EDGE,"E105.2.MirrorCS"),sQuery(id+"F4.wireOp",EDGE,"E105.3.MirrorCS"),sQuery(id+"F4.wireOp",EDGE,"E105.4.MirrorCS"),sQuery(id+"F4.wireOp",EDGE,"E105.5.MirrorCS"),sQuery(id+"F4.wireOp",EDGE,"E105.6.MirrorCS"),sQuery(id+"F4.wireOp",EDGE,"E105.7.MirrorCS"),sQuery(id+"F4.wireOp",EDGE,"E105.8.MirrorCS"),sQuery(id+"F4.wireOp",EDGE,"E105.9.MirrorCS"),sQuery(id+"F4.wireOp",EDGE,"E105.10.MirrorCS"),sQuery(id+"F4.wireOp",EDGE,"E105.11.MirrorCS"),sQuery(id+"F4.wireOp",EDGE,"E105.13.MirrorCS"),sQuery(id+"F4.wireOp",EDGE,"E105.14.MirrorCS"),sQuery(id+"F4.wireOp",EDGE,"E105.15.MirrorCS"),sQuery(id+"F4.wireOp",EDGE,"E105.16.MirrorCS"),sQuery(id+"F4.wireOp",EDGE,"E105.17.MirrorCS"),sQuery(id+"F4.wireOp",EDGE,"E106.0.MirrorCS"),sQuery(id+"F4.wireOp",EDGE,"E107.0.MirrorCS"),sQuery(id+"F4.wireOp",EDGE,"E108.filletArc"),sQuery(id+"F4.wireOp",EDGE,"E109.filletArc"),sQuery(id+"F4.wireOp",EDGE,"E110.filletArc"),sQuery(id+"F4.wireOp",EDGE,"E111.filletArc"),sQuery(id+"F4.wireOp",EDGE,"E113.filletArc"),sQuery(id+"F4.wireOp",EDGE,"E114.filletArc"),sQuery(id+"F4.wireOp",EDGE,"E115.filletArc"),sQuery(id+"F4.wireOp",EDGE,"E116.filletArc"),sQuery(id+"F4.wireOp",EDGE,"E117.filletArc"),sQuery(id+"F4.wireOp",EDGE,"E118.filletArc"),sQuery(id+"F4.wireOp",EDGE,"E119.filletArc"),sQuery(id+"F4.wireOp",EDGE,"E120.filletArc"),sQuery(id+"F4.wireOp",EDGE,"E124.filletArc"),sQuery(id+"F4.wireOp",EDGE,"E125.filletArc"),sQuery(id+"F4.wireOp",EDGE,"E126.filletArc"),sQuery(id+"F4.wireOp",EDGE,"E127.filletArc"),sQuery(id+"F4.wireOp",EDGE,"E128.filletArc"),sQuery(id+"F4.wireOp",EDGE,"E129.filletArc"),sQuery(id+"F4.wireOp",EDGE,"E130.filletArc"),sQuery(id+"F4.wireOp",EDGE,"E131.filletArc")])]});
            var Q1;
            Q1=qCreatedBy(makeId("Top.planeOp"),FACE);
            mirror(context, id + "F6", {"entities" : qUnion([Q0]), "mirrorPlane" : qUnion([Q1])});
        }
        {
            var Q0;
            Q0=qCreatedBy(makeId("Front.planeOp"),FACE);
            var sketch = newSketch(context, id + "F7", { "sketchPlane" : qUnion([Q0])});
            skCircle(sketch, "E132", {"center": v(165.1, 182.3) * mm, "radius": 2.5 * mm});
            skLineSegment(sketch, "E133", {"start": v(165.1, 182.3) * mm, "end": v(165.1, 186.35) * mm, "construction": true});
            skLineSegment(sketch, "E134", {"start": v(165.1, 182.3) * mm, "end": v(161.05, 182.3) * mm, "construction": true});
            skLineSegment(sketch, "E135", {"start": v(165.1, 182.3) * mm, "end": v(152.6, 194.8) * mm, "construction": true});
            skLineSegment(sketch, "E136", {"start": v(152.6, 192.66) * mm, "end": v(152.6, 186.62) * mm});
            skLineSegment(sketch, "E137", {"start": v(154.74, 194.8) * mm, "end": v(160.78, 194.8) * mm});
            skLineSegment(sketch, "E138", {"start": v(160.78, 192.66) * mm, "end": v(158.84, 192.66) * mm});
            skLineSegment(sketch, "E139", {"start": v(154.74, 188.56) * mm, "end": v(154.74, 186.62) * mm});
            skArc(sketch, "E140", {"start": v(160.78, 194.8) * mm, "mid": v(161.85, 193.73) * mm, "end": v(160.78, 192.66) * mm});
            skArc(sketch, "E141", {"start": v(154.74, 186.62) * mm, "mid": v(153.67, 185.55) * mm, "end": v(152.6, 186.62) * mm});
            skLineSegment(sketch, "E142", {"start": v(165.1, 186.35) * mm, "end": v(163, 186.35) * mm});
            skLineSegment(sketch, "E143", {"start": v(161.05, 184.4) * mm, "end": v(161.05, 182.3) * mm});
            skLineSegment(sketch, "E144", {"start": v(156.57, 189.32) * mm, "end": v(160.74, 185.15) * mm});
            skLineSegment(sketch, "E145", {"start": v(158.08, 190.83) * mm, "end": v(162.25, 186.66) * mm});
            skLineSegment(sketch, "E146.0.MirrorCS", {"start": v(175.46, 188.56) * mm, "end": v(175.46, 186.62) * mm});
            skLineSegment(sketch, "E146.1.MirrorCS", {"start": v(172.12, 190.83) * mm, "end": v(167.95, 186.66) * mm});
            skArc(sketch, "E146.2.MirrorCS", {"start": v(169.42, 194.8) * mm, "mid": v(168.35, 193.73) * mm, "end": v(169.42, 192.66) * mm});
            skArc(sketch, "E146.3.MirrorCS", {"start": v(175.46, 186.62) * mm, "mid": v(176.53, 185.55) * mm, "end": v(177.6, 186.62) * mm});
            skLineSegment(sketch, "E146.4.MirrorCS", {"start": v(175.46, 194.8) * mm, "end": v(169.42, 194.8) * mm});
            skLineSegment(sketch, "E146.5.MirrorCS", {"start": v(169.42, 192.66) * mm, "end": v(171.36, 192.66) * mm});
            skLineSegment(sketch, "E146.6.MirrorCS", {"start": v(177.6, 192.66) * mm, "end": v(177.6, 186.62) * mm});
            skLineSegment(sketch, "E146.7.MirrorCS", {"start": v(173.63, 189.32) * mm, "end": v(169.46, 185.15) * mm});
            skLineSegment(sketch, "E147.0.MirrorCS", {"start": v(165.1, 186.35) * mm, "end": v(167.2, 186.35) * mm});
            skLineSegment(sketch, "E148.0.MirrorCS", {"start": v(169.15, 184.4) * mm, "end": v(169.15, 182.3) * mm});
            skLineSegment(sketch, "E149.0.MirrorCS", {"start": v(175.46, 169.8) * mm, "end": v(169.42, 169.8) * mm});
            skLineSegment(sketch, "E149.1.MirrorCS", {"start": v(177.6, 171.94) * mm, "end": v(177.6, 177.98) * mm});
            skArc(sketch, "E149.2.MirrorCS", {"start": v(169.42, 169.8) * mm, "mid": v(168.35, 170.87) * mm, "end": v(169.42, 171.94) * mm});
            skLineSegment(sketch, "E149.3.MirrorCS", {"start": v(158.08, 173.77) * mm, "end": v(162.25, 177.94) * mm});
            skLineSegment(sketch, "E149.4.MirrorCS", {"start": v(172.12, 173.77) * mm, "end": v(167.95, 177.94) * mm});
            skLineSegment(sketch, "E149.5.MirrorCS", {"start": v(175.46, 176.04) * mm, "end": v(175.46, 177.98) * mm});
            skLineSegment(sketch, "E149.6.MirrorCS", {"start": v(173.63, 175.28) * mm, "end": v(169.46, 179.45) * mm});
            skLineSegment(sketch, "E149.7.MirrorCS", {"start": v(154.74, 169.8) * mm, "end": v(160.78, 169.8) * mm});
            skLineSegment(sketch, "E149.8.MirrorCS", {"start": v(160.78, 171.94) * mm, "end": v(158.84, 171.94) * mm});
            skLineSegment(sketch, "E149.9.MirrorCS", {"start": v(169.42, 171.94) * mm, "end": v(171.36, 171.94) * mm});
            skArc(sketch, "E149.10.MirrorCS", {"start": v(175.46, 177.98) * mm, "mid": v(176.53, 179.05) * mm, "end": v(177.6, 177.98) * mm});
            skLineSegment(sketch, "E149.11.MirrorCS", {"start": v(152.6, 171.94) * mm, "end": v(152.6, 177.98) * mm});
            skLineSegment(sketch, "E149.12.MirrorCS", {"start": v(165.1, 178.25) * mm, "end": v(167.2, 178.25) * mm});
            skArc(sketch, "E149.13.MirrorCS", {"start": v(160.78, 169.8) * mm, "mid": v(161.85, 170.87) * mm, "end": v(160.78, 171.94) * mm});
            skLineSegment(sketch, "E149.14.MirrorCS", {"start": v(156.57, 175.28) * mm, "end": v(160.74, 179.45) * mm});
            skArc(sketch, "E149.15.MirrorCS", {"start": v(154.74, 177.98) * mm, "mid": v(153.67, 179.05) * mm, "end": v(152.6, 177.98) * mm});
            skLineSegment(sketch, "E149.16.MirrorCS", {"start": v(154.74, 176.04) * mm, "end": v(154.74, 177.98) * mm});
            skLineSegment(sketch, "E149.17.MirrorCS", {"start": v(165.1, 178.25) * mm, "end": v(163, 178.25) * mm});
            skLineSegment(sketch, "E150.0.MirrorCS", {"start": v(169.15, 180.2) * mm, "end": v(169.15, 182.3) * mm});
            skLineSegment(sketch, "E151.0.MirrorCS", {"start": v(161.05, 180.2) * mm, "end": v(161.05, 182.3) * mm});
            skPoint(sketch, "E152.visualSharp", {"position": v(152.6, 194.8) * mm});
            skArc(sketch, "E152.filletArc", {"start": v(154.74, 194.8) * mm, "mid": v(153.23, 194.17) * mm, "end": v(152.6, 192.66) * mm});
            skPoint(sketch, "E153.visualSharp", {"position": v(177.6, 194.8) * mm});
            skArc(sketch, "E153.filletArc", {"start": v(177.6, 192.66) * mm, "mid": v(176.97, 194.17) * mm, "end": v(175.46, 194.8) * mm});
            skPoint(sketch, "E154.visualSharp", {"position": v(177.6, 169.8) * mm});
            skArc(sketch, "E154.filletArc", {"start": v(175.46, 169.8) * mm, "mid": v(176.97, 170.43) * mm, "end": v(177.6, 171.94) * mm});
            skPoint(sketch, "E155.visualSharp", {"position": v(152.6, 169.8) * mm});
            skArc(sketch, "E155.filletArc", {"start": v(152.6, 171.94) * mm, "mid": v(153.23, 170.43) * mm, "end": v(154.74, 169.8) * mm});
            skPoint(sketch, "E156.visualSharp", {"position": v(169.15, 186.35) * mm});
            skPoint(sketch, "E157.visualSharp", {"position": v(154.74, 191.15) * mm});
            skArc(sketch, "E157.filletArc", {"start": v(156.57, 189.32) * mm, "mid": v(155.4, 189.55) * mm, "end": v(154.74, 188.56) * mm});
            skPoint(sketch, "E158.visualSharp", {"position": v(156.25, 192.66) * mm});
            skArc(sketch, "E158.filletArc", {"start": v(158.84, 192.66) * mm, "mid": v(157.85, 192) * mm, "end": v(158.08, 190.83) * mm});
            skPoint(sketch, "E159.visualSharp", {"position": v(173.95, 192.66) * mm});
            skArc(sketch, "E159.filletArc", {"start": v(172.12, 190.83) * mm, "mid": v(172.35, 192) * mm, "end": v(171.36, 192.66) * mm});
            skPoint(sketch, "E160.visualSharp", {"position": v(175.46, 191.15) * mm});
            skArc(sketch, "E160.filletArc", {"start": v(175.46, 188.56) * mm, "mid": v(174.8, 189.55) * mm, "end": v(173.63, 189.32) * mm});
            skPoint(sketch, "E161.visualSharp", {"position": v(175.46, 173.45) * mm});
            skArc(sketch, "E161.filletArc", {"start": v(173.63, 175.28) * mm, "mid": v(174.8, 175.05) * mm, "end": v(175.46, 176.04) * mm});
            skPoint(sketch, "E162.visualSharp", {"position": v(173.95, 171.94) * mm});
            skArc(sketch, "E162.filletArc", {"start": v(171.36, 171.94) * mm, "mid": v(172.35, 172.6) * mm, "end": v(172.12, 173.77) * mm});
            skPoint(sketch, "E163.visualSharp", {"position": v(156.25, 171.94) * mm});
            skArc(sketch, "E163.filletArc", {"start": v(158.08, 173.77) * mm, "mid": v(157.85, 172.6) * mm, "end": v(158.84, 171.94) * mm});
            skPoint(sketch, "E164.visualSharp", {"position": v(154.74, 173.45) * mm});
            skArc(sketch, "E164.filletArc", {"start": v(154.74, 176.04) * mm, "mid": v(155.4, 175.05) * mm, "end": v(156.57, 175.28) * mm});
            skPoint(sketch, "E165.orphan", {"position": v(161.05, 186.35) * mm});
            skPoint(sketch, "E166.orphan", {"position": v(169.15, 178.25) * mm});
            skPoint(sketch, "E167.orphan", {"position": v(161.05, 178.25) * mm});
            skPoint(sketch, "E168.visualSharp", {"position": v(162.56, 186.35) * mm});
            skArc(sketch, "E168.filletArc", {"start": v(162.25, 186.66) * mm, "mid": v(162.6, 186.43) * mm, "end": v(163, 186.35) * mm});
            skPoint(sketch, "E169.visualSharp", {"position": v(167.64, 186.35) * mm});
            skArc(sketch, "E169.filletArc", {"start": v(167.2, 186.35) * mm, "mid": v(167.6, 186.43) * mm, "end": v(167.95, 186.66) * mm});
            skPoint(sketch, "E170.visualSharp", {"position": v(161.05, 184.84) * mm});
            skArc(sketch, "E170.filletArc", {"start": v(161.05, 184.4) * mm, "mid": v(160.97, 184.8) * mm, "end": v(160.74, 185.15) * mm});
            skPoint(sketch, "E171.visualSharp", {"position": v(161.05, 179.76) * mm});
            skArc(sketch, "E171.filletArc", {"start": v(160.74, 179.45) * mm, "mid": v(160.97, 179.8) * mm, "end": v(161.05, 180.2) * mm});
            skPoint(sketch, "E172.visualSharp", {"position": v(162.56, 178.25) * mm});
            skArc(sketch, "E172.filletArc", {"start": v(163, 178.25) * mm, "mid": v(162.6, 178.17) * mm, "end": v(162.25, 177.94) * mm});
            skPoint(sketch, "E173.visualSharp", {"position": v(167.64, 178.25) * mm});
            skArc(sketch, "E173.filletArc", {"start": v(167.95, 177.94) * mm, "mid": v(167.6, 178.17) * mm, "end": v(167.2, 178.25) * mm});
            skPoint(sketch, "E174.visualSharp", {"position": v(169.15, 179.76) * mm});
            skArc(sketch, "E174.filletArc", {"start": v(169.15, 180.2) * mm, "mid": v(169.23, 179.8) * mm, "end": v(169.46, 179.45) * mm});
            skPoint(sketch, "E175.visualSharp", {"position": v(169.15, 184.84) * mm});
            skArc(sketch, "E175.filletArc", {"start": v(169.46, 185.15) * mm, "mid": v(169.23, 184.8) * mm, "end": v(169.15, 184.4) * mm});
            skLineSegment(sketch, "E176.0", {"start": v(12.5, 144.8) * mm, "end": v(317.7, 144.8) * mm, "construction": true});
            skLineSegment(sketch, "E177.0", {"start": v(12.5, 169.8) * mm, "end": v(317.7, 169.8) * mm, "construction": true});
            skLineSegment(sketch, "E178", {"start": v(165.1, 144.8) * mm, "end": v(165.1, -43.5) * mm, "construction": true});
            skSolve(sketch);
        }
        {
            var Q0;
            Q0=makeQuery(id+"F7.imprint","IMPRINT",FACE,{"disambiguationData":[TD([[makeQuery(id+"F7.imprint","IMPRINT",EDGE,{"derivedFrom":sQuery(id+"F7.wireOp",EDGE,"E132")}),-1.0]])]});
            var Q1;
            Q1=makeQuery(id+"F6.opPattern","COPY",FACE,{"derivedFrom":makeQuery(id+"F5.opExtrude","SWEPT_FACE",FACE,{"disambiguationData":[OSD([sQuery(id+"F4.wireOp",EDGE,"E105.11.MirrorCS")])]}),"instanceName":"1"});
            extrude(context, id + "F8", {"entities" : qUnion([Q0]), "depth" : 340 * mm, "hasSecondDirection" : true, "secondDirectionBound" : SecondDirectionBoundingType.UP_TO_SURFACE, "secondDirectionOppositeDirection" : true, "secondDirectionBoundEntityFace" : qUnion([Q1]), "secondDirectionDepth" : 25.4 * mm});
        }
        {
            var Q0;
            Q0=makeQuery(id+"F8.opExtrude","SWEPT_BODY",BODY,{"disambiguationData":[OSD([sQuery(id+"F7.wireOp",EDGE,"E132"),sQuery(id+"F7.wireOp",EDGE,"E136"),sQuery(id+"F7.wireOp",EDGE,"E137"),sQuery(id+"F7.wireOp",EDGE,"E138"),sQuery(id+"F7.wireOp",EDGE,"E139"),sQuery(id+"F7.wireOp",EDGE,"E140"),sQuery(id+"F7.wireOp",EDGE,"E141"),sQuery(id+"F7.wireOp",EDGE,"E143"),sQuery(id+"F7.wireOp",EDGE,"E144"),sQuery(id+"F7.wireOp",EDGE,"E145"),sQuery(id+"F7.wireOp",EDGE,"E146.0.MirrorCS"),sQuery(id+"F7.wireOp",EDGE,"E146.1.MirrorCS"),sQuery(id+"F7.wireOp",EDGE,"E146.2.MirrorCS"),sQuery(id+"F7.wireOp",EDGE,"E146.3.MirrorCS"),sQuery(id+"F7.wireOp",EDGE,"E146.4.MirrorCS"),sQuery(id+"F7.wireOp",EDGE,"E146.5.MirrorCS"),sQuery(id+"F7.wireOp",EDGE,"E146.6.MirrorCS"),sQuery(id+"F7.wireOp",EDGE,"E146.7.MirrorCS"),sQuery(id+"F7.wireOp",EDGE,"E147.0.MirrorCS"),sQuery(id+"F7.wireOp",EDGE,"E149.0.MirrorCS"),sQuery(id+"F7.wireOp",EDGE,"E149.1.MirrorCS"),sQuery(id+"F7.wireOp",EDGE,"E149.2.MirrorCS"),sQuery(id+"F7.wireOp",EDGE,"E149.3.MirrorCS"),sQuery(id+"F7.wireOp",EDGE,"E149.4.MirrorCS"),sQuery(id+"F7.wireOp",EDGE,"E149.5.MirrorCS"),sQuery(id+"F7.wireOp",EDGE,"E149.6.MirrorCS"),sQuery(id+"F7.wireOp",EDGE,"E149.7.MirrorCS"),sQuery(id+"F7.wireOp",EDGE,"E149.8.MirrorCS"),sQuery(id+"F7.wireOp",EDGE,"E149.9.MirrorCS"),sQuery(id+"F7.wireOp",EDGE,"E149.10.MirrorCS"),sQuery(id+"F7.wireOp",EDGE,"E149.11.MirrorCS"),sQuery(id+"F7.wireOp",EDGE,"E149.13.MirrorCS"),sQuery(id+"F7.wireOp",EDGE,"E149.14.MirrorCS"),sQuery(id+"F7.wireOp",EDGE,"E149.15.MirrorCS"),sQuery(id+"F7.wireOp",EDGE,"E149.16.MirrorCS"),sQuery(id+"F7.wireOp",EDGE,"E149.17.MirrorCS"),sQuery(id+"F7.wireOp",EDGE,"E150.0.MirrorCS"),sQuery(id+"F7.wireOp",EDGE,"E152.filletArc"),sQuery(id+"F7.wireOp",EDGE,"E153.filletArc"),sQuery(id+"F7.wireOp",EDGE,"E154.filletArc"),sQuery(id+"F7.wireOp",EDGE,"E155.filletArc"),sQuery(id+"F7.wireOp",EDGE,"E157.filletArc"),sQuery(id+"F7.wireOp",EDGE,"E158.filletArc"),sQuery(id+"F7.wireOp",EDGE,"E159.filletArc"),sQuery(id+"F7.wireOp",EDGE,"E160.filletArc"),sQuery(id+"F7.wireOp",EDGE,"E161.filletArc"),sQuery(id+"F7.wireOp",EDGE,"E162.filletArc"),sQuery(id+"F7.wireOp",EDGE,"E163.filletArc"),sQuery(id+"F7.wireOp",EDGE,"E164.filletArc"),sQuery(id+"F7.wireOp",EDGE,"E168.filletArc"),sQuery(id+"F7.wireOp",EDGE,"E169.filletArc"),sQuery(id+"F7.wireOp",EDGE,"E170.filletArc"),sQuery(id+"F7.wireOp",EDGE,"E171.filletArc"),sQuery(id+"F7.wireOp",EDGE,"E172.filletArc"),sQuery(id+"F7.wireOp",EDGE,"E173.filletArc"),sQuery(id+"F7.wireOp",EDGE,"E174.filletArc"),sQuery(id+"F7.wireOp",EDGE,"E175.filletArc")])]});
            var Q1;
            Q1=qCreatedBy(makeId("Top.planeOp"),FACE);
            mirror(context, id + "F9", {"entities" : qUnion([Q0]), "mirrorPlane" : qUnion([Q1])});
        }
        {
            var Q0;
            Q0=makeQuery(id+"F8.opExtrude","SWEPT_FACE",FACE,{"disambiguationData":[OSD([sQuery(id+"F7.wireOp",EDGE,"E149.7.MirrorCS")])]});
            var sketch = newSketch(context, id + "F10", { "sketchPlane" : qUnion([Q0])});
            skCircle(sketch, "E179", {"center": v(165.1, 327.5) * mm, "radius": 2.5 * mm});
            skLineSegment(sketch, "E180", {"start": v(165.1, 327.5) * mm, "end": v(165.1, 331.55) * mm, "construction": true});
            skLineSegment(sketch, "E181", {"start": v(165.1, 327.5) * mm, "end": v(161.05, 327.5) * mm, "construction": true});
            skLineSegment(sketch, "E182", {"start": v(165.1, 327.5) * mm, "end": v(152.6, 340) * mm, "construction": true});
            skLineSegment(sketch, "E183", {"start": v(152.6, 337.86) * mm, "end": v(152.6, 331.82) * mm});
            skLineSegment(sketch, "E184", {"start": v(154.74, 340) * mm, "end": v(160.78, 340) * mm});
            skLineSegment(sketch, "E185", {"start": v(160.78, 337.86) * mm, "end": v(158.84, 337.86) * mm});
            skLineSegment(sketch, "E186", {"start": v(154.74, 333.76) * mm, "end": v(154.74, 331.82) * mm});
            skArc(sketch, "E187", {"start": v(160.78, 340) * mm, "mid": v(161.85, 338.93) * mm, "end": v(160.78, 337.86) * mm});
            skArc(sketch, "E188", {"start": v(154.74, 331.82) * mm, "mid": v(153.67, 330.75) * mm, "end": v(152.6, 331.82) * mm});
            skLineSegment(sketch, "E189", {"start": v(165.1, 331.55) * mm, "end": v(163, 331.55) * mm});
            skLineSegment(sketch, "E190", {"start": v(161.05, 329.6) * mm, "end": v(161.05, 327.5) * mm});
            skLineSegment(sketch, "E191", {"start": v(156.57, 334.52) * mm, "end": v(160.74, 330.35) * mm});
            skLineSegment(sketch, "E192", {"start": v(158.08, 336.03) * mm, "end": v(162.25, 331.86) * mm});
            skLineSegment(sketch, "E193.0.MirrorCS", {"start": v(175.46, 333.76) * mm, "end": v(175.46, 331.82) * mm});
            skLineSegment(sketch, "E193.1.MirrorCS", {"start": v(172.12, 336.03) * mm, "end": v(167.95, 331.86) * mm});
            skArc(sketch, "E193.2.MirrorCS", {"start": v(169.42, 340) * mm, "mid": v(168.35, 338.93) * mm, "end": v(169.42, 337.86) * mm});
            skArc(sketch, "E193.3.MirrorCS", {"start": v(175.46, 331.82) * mm, "mid": v(176.53, 330.75) * mm, "end": v(177.6, 331.82) * mm});
            skLineSegment(sketch, "E193.4.MirrorCS", {"start": v(175.46, 340) * mm, "end": v(169.42, 340) * mm});
            skLineSegment(sketch, "E193.5.MirrorCS", {"start": v(169.42, 337.86) * mm, "end": v(171.36, 337.86) * mm});
            skLineSegment(sketch, "E193.6.MirrorCS", {"start": v(177.6, 337.86) * mm, "end": v(177.6, 331.82) * mm});
            skLineSegment(sketch, "E193.7.MirrorCS", {"start": v(173.63, 334.52) * mm, "end": v(169.46, 330.35) * mm});
            skLineSegment(sketch, "E194.0.MirrorCS", {"start": v(165.1, 331.55) * mm, "end": v(167.2, 331.55) * mm});
            skLineSegment(sketch, "E195.0.MirrorCS", {"start": v(169.15, 329.6) * mm, "end": v(169.15, 327.5) * mm});
            skLineSegment(sketch, "E196.0.MirrorCS", {"start": v(175.46, 315) * mm, "end": v(169.42, 315) * mm});
            skLineSegment(sketch, "E196.1.MirrorCS", {"start": v(177.6, 317.14) * mm, "end": v(177.6, 323.18) * mm});
            skArc(sketch, "E196.2.MirrorCS", {"start": v(169.42, 315) * mm, "mid": v(168.35, 316.07) * mm, "end": v(169.42, 317.14) * mm});
            skLineSegment(sketch, "E196.3.MirrorCS", {"start": v(158.08, 318.97) * mm, "end": v(162.25, 323.14) * mm});
            skLineSegment(sketch, "E196.4.MirrorCS", {"start": v(172.12, 318.97) * mm, "end": v(167.95, 323.14) * mm});
            skLineSegment(sketch, "E196.5.MirrorCS", {"start": v(175.46, 321.24) * mm, "end": v(175.46, 323.18) * mm});
            skLineSegment(sketch, "E196.6.MirrorCS", {"start": v(173.63, 320.48) * mm, "end": v(169.46, 324.65) * mm});
            skLineSegment(sketch, "E196.7.MirrorCS", {"start": v(154.74, 315) * mm, "end": v(160.78, 315) * mm});
            skLineSegment(sketch, "E196.8.MirrorCS", {"start": v(160.78, 317.14) * mm, "end": v(158.84, 317.14) * mm});
            skLineSegment(sketch, "E196.9.MirrorCS", {"start": v(169.42, 317.14) * mm, "end": v(171.36, 317.14) * mm});
            skArc(sketch, "E196.10.MirrorCS", {"start": v(175.46, 323.18) * mm, "mid": v(176.53, 324.25) * mm, "end": v(177.6, 323.18) * mm});
            skLineSegment(sketch, "E196.11.MirrorCS", {"start": v(152.6, 317.14) * mm, "end": v(152.6, 323.18) * mm});
            skLineSegment(sketch, "E196.12.MirrorCS", {"start": v(165.1, 323.45) * mm, "end": v(167.2, 323.45) * mm});
            skArc(sketch, "E196.13.MirrorCS", {"start": v(160.78, 315) * mm, "mid": v(161.85, 316.07) * mm, "end": v(160.78, 317.14) * mm});
            skLineSegment(sketch, "E196.14.MirrorCS", {"start": v(156.57, 320.48) * mm, "end": v(160.74, 324.65) * mm});
            skArc(sketch, "E196.15.MirrorCS", {"start": v(154.74, 323.18) * mm, "mid": v(153.67, 324.25) * mm, "end": v(152.6, 323.18) * mm});
            skLineSegment(sketch, "E196.16.MirrorCS", {"start": v(154.74, 321.24) * mm, "end": v(154.74, 323.18) * mm});
            skLineSegment(sketch, "E196.17.MirrorCS", {"start": v(165.1, 323.45) * mm, "end": v(163, 323.45) * mm});
            skLineSegment(sketch, "E197.0.MirrorCS", {"start": v(169.15, 325.4) * mm, "end": v(169.15, 327.5) * mm});
            skLineSegment(sketch, "E198.0.MirrorCS", {"start": v(161.05, 325.4) * mm, "end": v(161.05, 327.5) * mm});
            skPoint(sketch, "E199.visualSharp", {"position": v(152.6, 340) * mm});
            skArc(sketch, "E199.filletArc", {"start": v(154.74, 340) * mm, "mid": v(153.23, 339.37) * mm, "end": v(152.6, 337.86) * mm});
            skPoint(sketch, "E200.visualSharp", {"position": v(177.6, 340) * mm});
            skArc(sketch, "E200.filletArc", {"start": v(177.6, 337.86) * mm, "mid": v(176.97, 339.37) * mm, "end": v(175.46, 340) * mm});
            skPoint(sketch, "E201.visualSharp", {"position": v(177.6, 315) * mm});
            skArc(sketch, "E201.filletArc", {"start": v(175.46, 315) * mm, "mid": v(176.97, 315.63) * mm, "end": v(177.6, 317.14) * mm});
            skPoint(sketch, "E202.visualSharp", {"position": v(152.6, 315) * mm});
            skArc(sketch, "E202.filletArc", {"start": v(152.6, 317.14) * mm, "mid": v(153.23, 315.63) * mm, "end": v(154.74, 315) * mm});
            skPoint(sketch, "E203.visualSharp", {"position": v(169.15, 331.55) * mm});
            skPoint(sketch, "E204.visualSharp", {"position": v(154.74, 336.35) * mm});
            skArc(sketch, "E204.filletArc", {"start": v(156.57, 334.52) * mm, "mid": v(155.4, 334.75) * mm, "end": v(154.74, 333.76) * mm});
            skPoint(sketch, "E205.visualSharp", {"position": v(156.25, 337.86) * mm});
            skArc(sketch, "E205.filletArc", {"start": v(158.84, 337.86) * mm, "mid": v(157.85, 337.2) * mm, "end": v(158.08, 336.03) * mm});
            skPoint(sketch, "E206.visualSharp", {"position": v(173.95, 337.86) * mm});
            skArc(sketch, "E206.filletArc", {"start": v(172.12, 336.03) * mm, "mid": v(172.35, 337.2) * mm, "end": v(171.36, 337.86) * mm});
            skPoint(sketch, "E207.visualSharp", {"position": v(175.46, 336.35) * mm});
            skArc(sketch, "E207.filletArc", {"start": v(175.46, 333.76) * mm, "mid": v(174.8, 334.75) * mm, "end": v(173.63, 334.52) * mm});
            skPoint(sketch, "E208.visualSharp", {"position": v(175.46, 318.65) * mm});
            skArc(sketch, "E208.filletArc", {"start": v(173.63, 320.48) * mm, "mid": v(174.8, 320.25) * mm, "end": v(175.46, 321.24) * mm});
            skPoint(sketch, "E209.visualSharp", {"position": v(173.95, 317.14) * mm});
            skArc(sketch, "E209.filletArc", {"start": v(171.36, 317.14) * mm, "mid": v(172.35, 317.8) * mm, "end": v(172.12, 318.97) * mm});
            skPoint(sketch, "E210.visualSharp", {"position": v(156.25, 317.14) * mm});
            skArc(sketch, "E210.filletArc", {"start": v(158.08, 318.97) * mm, "mid": v(157.85, 317.8) * mm, "end": v(158.84, 317.14) * mm});
            skPoint(sketch, "E211.visualSharp", {"position": v(154.74, 318.65) * mm});
            skArc(sketch, "E211.filletArc", {"start": v(154.74, 321.24) * mm, "mid": v(155.4, 320.25) * mm, "end": v(156.57, 320.48) * mm});
            skPoint(sketch, "E212.orphan", {"position": v(161.05, 331.55) * mm});
            skPoint(sketch, "E213.orphan", {"position": v(169.15, 323.45) * mm});
            skPoint(sketch, "E214.orphan", {"position": v(161.05, 323.45) * mm});
            skPoint(sketch, "E215.visualSharp", {"position": v(162.56, 331.55) * mm});
            skArc(sketch, "E215.filletArc", {"start": v(162.25, 331.86) * mm, "mid": v(162.6, 331.63) * mm, "end": v(163, 331.55) * mm});
            skPoint(sketch, "E216.visualSharp", {"position": v(167.64, 331.55) * mm});
            skArc(sketch, "E216.filletArc", {"start": v(167.2, 331.55) * mm, "mid": v(167.6, 331.63) * mm, "end": v(167.95, 331.86) * mm});
            skPoint(sketch, "E217.visualSharp", {"position": v(161.05, 330.04) * mm});
            skArc(sketch, "E217.filletArc", {"start": v(161.05, 329.6) * mm, "mid": v(160.97, 330) * mm, "end": v(160.74, 330.35) * mm});
            skPoint(sketch, "E218.visualSharp", {"position": v(161.05, 324.96) * mm});
            skArc(sketch, "E218.filletArc", {"start": v(160.74, 324.65) * mm, "mid": v(160.97, 325) * mm, "end": v(161.05, 325.4) * mm});
            skPoint(sketch, "E219.visualSharp", {"position": v(162.56, 323.45) * mm});
            skArc(sketch, "E219.filletArc", {"start": v(163, 323.45) * mm, "mid": v(162.6, 323.37) * mm, "end": v(162.25, 323.14) * mm});
            skPoint(sketch, "E220.visualSharp", {"position": v(167.64, 323.45) * mm});
            skArc(sketch, "E220.filletArc", {"start": v(167.95, 323.14) * mm, "mid": v(167.6, 323.37) * mm, "end": v(167.2, 323.45) * mm});
            skPoint(sketch, "E221.visualSharp", {"position": v(169.15, 324.96) * mm});
            skArc(sketch, "E221.filletArc", {"start": v(169.15, 325.4) * mm, "mid": v(169.23, 325) * mm, "end": v(169.46, 324.65) * mm});
            skPoint(sketch, "E222.visualSharp", {"position": v(169.15, 330.04) * mm});
            skArc(sketch, "E222.filletArc", {"start": v(169.46, 330.35) * mm, "mid": v(169.23, 330) * mm, "end": v(169.15, 329.6) * mm});
            skLineSegment(sketch, "E223.0", {"start": v(167.2, -12.57) * mm, "end": v(163, -12.57) * mm, "construction": true});
            skLineSegment(sketch, "E224", {"start": v(165.1, -12.57) * mm, "end": v(165.1, 425.14) * mm, "construction": true});
            skSolve(sketch);
        }
        {
            var Q0;
            Q0=qSketchRegion(id+"F10",true);
            extrude(context, id + "F11", {"entities" : qUnion([Q0]), "depth" : 340 * mm});
        }
    });
